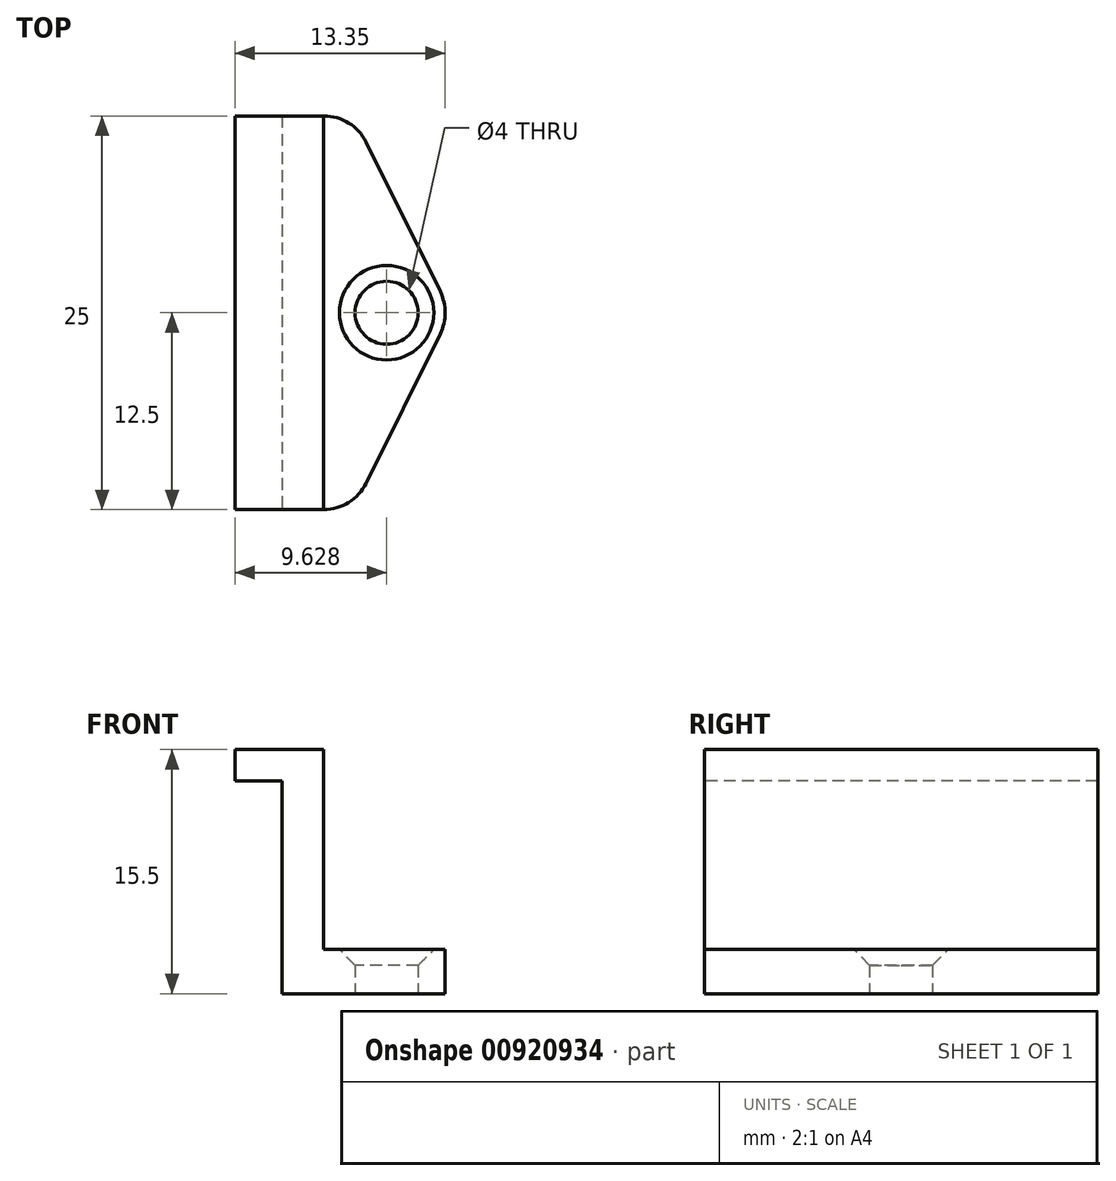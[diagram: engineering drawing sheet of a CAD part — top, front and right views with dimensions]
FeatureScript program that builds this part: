
annotation { "Feature Type Name" : "Feature", "Feature Type Description" : "" }
export const myFeature = defineFeature(function(context is Context, id is Id, definition is map)
    precondition{}
    {
        {
            var Q0;
            Q0=qCreatedBy(makeId("Top.planeOp"),FACE);
            var sketch = newSketch(context, id + "F0", { "sketchPlane" : qUnion([Q0])});
            skLineSegment(sketch, "E0", {"start": v(0, 0) * mm, "end": v(9.2, 0) * mm});
            skLineSegment(sketch, "E1", {"start": v(9.2, 0) * mm, "end": v(3, 12.5) * mm});
            skLineSegment(sketch, "E2", {"start": v(3, 12.5) * mm, "end": v(0, 12.5) * mm});
            skLineSegment(sketch, "E3", {"start": v(0, 12.5) * mm, "end": v(0, -12.5) * mm});
            skLineSegment(sketch, "E4", {"start": v(0, -12.5) * mm, "end": v(3, -12.5) * mm});
            skLineSegment(sketch, "E5", {"start": v(3, -12.5) * mm, "end": v(9.2, 0) * mm});
            skCircle(sketch, "E6", {"center": v(5.13, 0) * mm, "radius": 2 * mm});
            skSolve(sketch);
        }
        {
            var Q0;
            {var subQ3=sQuery(id+"F0.wireOp",EDGE,"E4");Q0=makeQuery(id+"F0.imprint","IMPRINT",FACE,{"disambiguationData":[TD([[makeQuery(id+"F0.imprint","IMPRINT",EDGE,{"derivedFrom":subQ3}),1.0]])]});}
            var Q1;
            {var subQ1=sQuery(id+"F0.wireOp",EDGE,"E1");Q1=makeQuery(id+"F0.imprint","IMPRINT",FACE,{"disambiguationData":[TD([[makeQuery(id+"F0.imprint","IMPRINT",EDGE,{"derivedFrom":subQ1}),1.0]])]});}
            extrude(context, id + "F1", {"entities" : qUnion([Q0, Q1]), "depth" : 2.8 * mm, "offsetDistance" : 25 * mm});
        }
        {
            var Q0;
            Q0=makeQuery(id+"F1.opExtrude","SWEPT_EDGE",EDGE,{"disambiguationData":[OSD([sQuery(id+"F0.wireOp",EDGE,"E0"),sQuery(id+"F0.wireOp",EDGE,"E1"),sQuery(id+"F0.wireOp",EDGE,"E5")])]});
            var Q1;
            Q1=makeQuery(id+"F1.opExtrude","SWEPT_EDGE",EDGE,{"disambiguationData":[OSD([sQuery(id+"F0.wireOp",EDGE,"E4"),sQuery(id+"F0.wireOp",EDGE,"E5")])]});
            var Q2;
            Q2=makeQuery(id+"F1.opExtrude","SWEPT_EDGE",EDGE,{"disambiguationData":[OSD([sQuery(id+"F0.wireOp",EDGE,"E1"),sQuery(id+"F0.wireOp",EDGE,"E2")])]});
            fillet(context, id + "F2", {"entities" : qUnion([Q0, Q1, Q2]), "radius" : 3 * mm, "tangentPropagation" : true, "allowEdgeOverflow" : false});
        }
        {
            var Q0;
            Q0=makeQuery(id+"F1.opExtrude","CAP_EDGE",EDGE,{"disambiguationData":[OSD([sQuery(id+"F0.wireOp",EDGE,"E6")])],"isStart":false});
            chamfer(context, id + "F3", {"entities" : qUnion([Q0]), "width" : 1 * mm, "tangentPropagation" : true});
        }
        {
            var Q0;
            Q0=makeQuery(id+"F1.opExtrude","SWEPT_FACE",FACE,{"disambiguationData":[OSD([sQuery(id+"F0.wireOp",EDGE,"E3")])]});
            extrude(context, id + "F4", {"entities" : qUnion([Q0]), "operationType" : NewBodyOperationType.ADD, "depth" : 1.5 * mm, "offsetDistance" : 25 * mm});
        }
        {
            var Q0;
            {var subQ0=sQuery(id+"F0.wireOp",EDGE,"E3");Q0=makeQuery(id+"F4.boolean.opBoolean","MERGE",FACE,{"derivedFrom":[makeQuery(id+"F1.opExtrude","CAP_FACE",FACE,{"disambiguationData":[OSD([sQuery(id+"F0.wireOp",EDGE,"E1"),sQuery(id+"F0.wireOp",EDGE,"E2"),subQ0,sQuery(id+"F0.wireOp",EDGE,"E4"),sQuery(id+"F0.wireOp",EDGE,"E5"),sQuery(id+"F0.wireOp",EDGE,"E6")])],"isStart":false}),makeQuery(id+"F4.opExtrude","SWEPT_FACE",FACE,{"disambiguationData":[OSD([subQ0]),TDD([makeQuery(id+"F1.opExtrude","CAP_EDGE",EDGE,{"disambiguationData":[OSD([subQ0])],"isStart":false})])]})]});}
            var sketch = newSketch(context, id + "F5", { "sketchPlane" : qUnion([Q0])});
            skLineSegment(sketch, "E7.bottom", {"start": v(-1.5, 12.5) * mm, "end": v(1.14, 12.5) * mm});
            skLineSegment(sketch, "E7.top", {"start": v(-1.5, -12.5) * mm, "end": v(1.14, -12.5) * mm});
            skLineSegment(sketch, "E7.left", {"start": v(-1.5, 12.5) * mm, "end": v(-1.5, -12.5) * mm});
            skLineSegment(sketch, "E7.right", {"start": v(1.14, 12.5) * mm, "end": v(1.14, -12.5) * mm});
            skSolve(sketch);
        }
        {
            var Q0;
            Q0=makeQuery(id+"F5.imprint","IMPRINT",FACE,{"disambiguationData":[TD([[makeQuery(id+"F5.imprint","IMPRINT",EDGE,{"derivedFrom":sQuery(id+"F5.wireOp",EDGE,"E7.bottom")}),1.0]])]});
            extrude(context, id + "F6", {"entities" : qUnion([Q0]), "operationType" : NewBodyOperationType.ADD, "depth" : 12.7 * mm, "offsetDistance" : 25 * mm});
        }
        {
            var Q0;
            Q0=makeQuery(id+"F6.boolean.opBoolean","MERGE",FACE,{"derivedFrom":[makeQuery(id+"F4.opExtrude","CAP_FACE",FACE,{"disambiguationData":[OSD([sQuery(id+"F0.wireOp",EDGE,"E3")])],"isStart":false}),makeQuery(id+"F6.opExtrude","SWEPT_FACE",FACE,{"disambiguationData":[OSD([sQuery(id+"F5.wireOp",EDGE,"E7.left")])]})]});
            var sketch = newSketch(context, id + "F7", { "sketchPlane" : qUnion([Q0])});
            skLineSegment(sketch, "E8.bottom", {"start": v(-12.5, 15.5) * mm, "end": v(12.5, 15.5) * mm});
            skLineSegment(sketch, "E8.top", {"start": v(-12.5, 13.51) * mm, "end": v(12.5, 13.51) * mm});
            skLineSegment(sketch, "E8.left", {"start": v(-12.5, 15.5) * mm, "end": v(-12.5, 13.51) * mm});
            skLineSegment(sketch, "E8.right", {"start": v(12.5, 15.5) * mm, "end": v(12.5, 13.51) * mm});
            skSolve(sketch);
        }
        {
            var Q0;
            Q0 = qSketchRegion(id + "F7", true);
            extrude(context, id + "F8", {"entities" : qUnion([Q0]), "operationType" : NewBodyOperationType.ADD, "depth" : 3 * mm, "offsetDistance" : 25 * mm});
        }
    });
